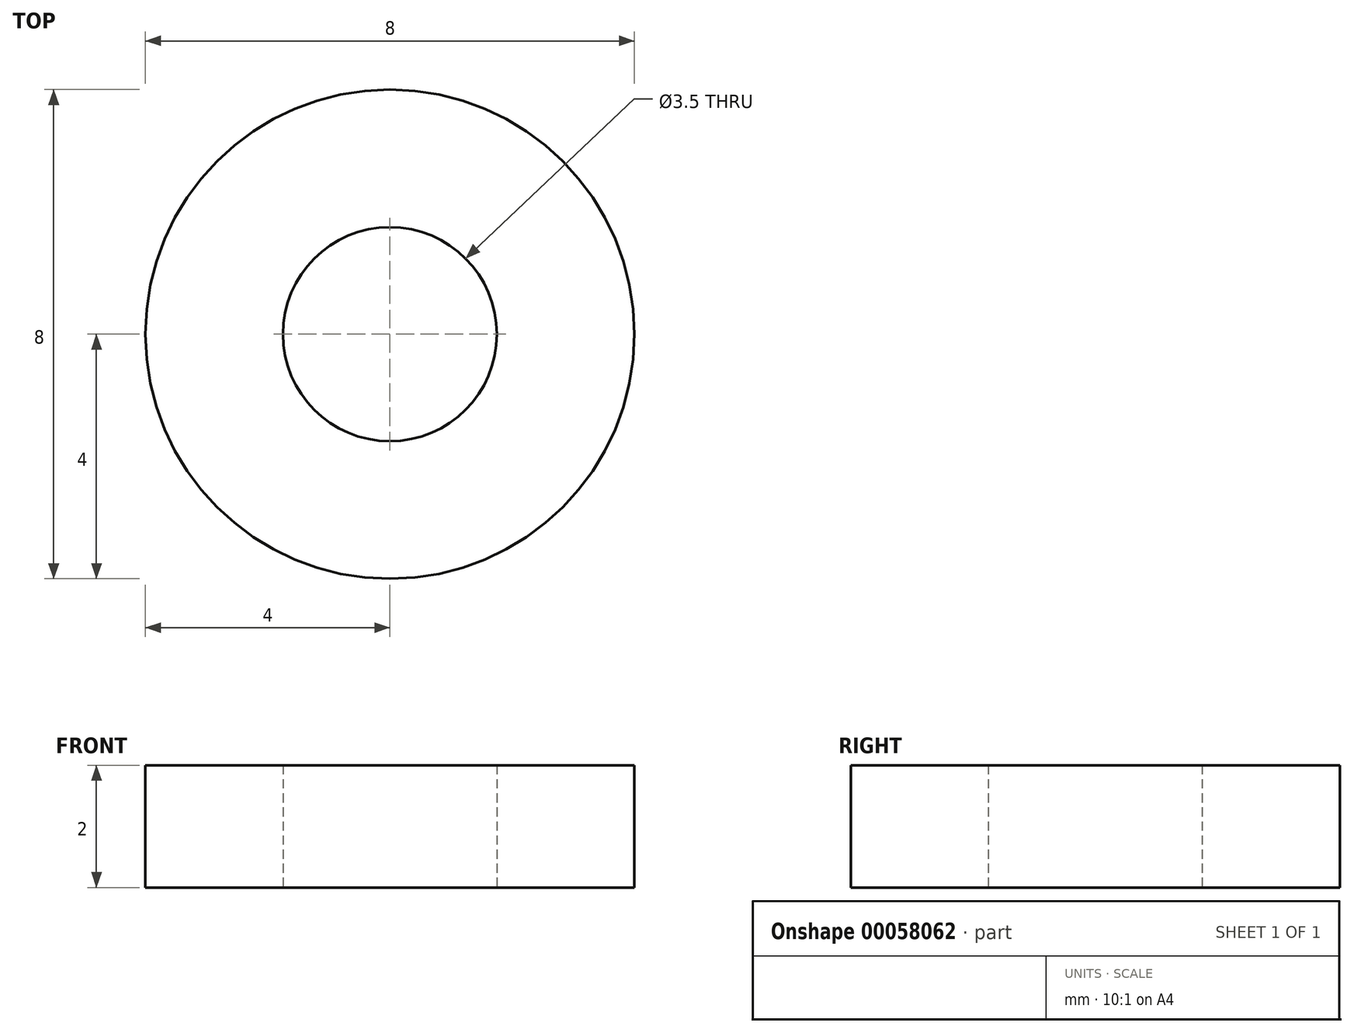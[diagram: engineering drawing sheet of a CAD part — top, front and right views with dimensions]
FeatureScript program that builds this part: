
annotation { "Feature Type Name" : "Feature", "Feature Type Description" : "" }
export const myFeature = defineFeature(function(context is Context, id is Id, definition is map)
    precondition{}
    {
        {
            var Q0;
            Q0=qCreatedBy(makeId("Top.planeOp"),FACE);
            var sketch = newSketch(context, id + "F0", { "sketchPlane" : qUnion([Q0])});
            skCircle(sketch, "E0", {"center": v(0, 0) * mm, "radius": 1.75 * mm});
            skCircle(sketch, "E1", {"center": v(0, 0) * mm, "radius": 4 * mm});
            skSolve(sketch);
        }
        {
            var Q0;
            Q0=makeQuery(id+"F0.imprint","IMPRINT",FACE,{"disambiguationData":[TD([[makeQuery(id+"F0.imprint","IMPRINT",EDGE,{"derivedFrom":sQuery(id+"F0.wireOp",EDGE,"E0")}),-1.0]])]});
            extrude(context, id + "F1", {"entities" : qUnion([Q0]), "depth" : 2 * mm});
        }
    });
